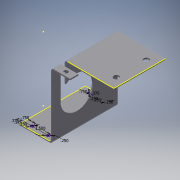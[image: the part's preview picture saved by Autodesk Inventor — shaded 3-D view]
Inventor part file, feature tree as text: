
AUTODESK INVENTOR PART (.ipt)
format: ipt  version: 2016 (Build 200138000, 138)  size: 217,088 bytes
history: native  units: in
note: dims shown in document units (in); Inventor stores cm internally (conversion verified against a paired STEP export)
features: sketch x12, sheet_metal_op x10, other x10, hole x1
ambient origin geometry x8: Origin, YZ Plane, XZ Plane, XY Plane, X Axis, Y Axis, Z Axis, Center Point
bodies: Solid1 (feature_tree)
feature tree (33):
  sheet_metal_op  "Face1"
  sheet_metal_op  "Flange1"
  sheet_metal_op  "Flange2"
  sketch  "Sketch6"  dims[d6=0.12in]
  sheet_metal_op  "Flange3"
  sketch  "Sketch11"  dims[d13=3.0in]
  sketch  "Sketch12"  dims[d14=3.75in d15=3.0in d16=0.12in d17=0.0in d18=0.5in d19=0.12in d20=0.0in d21=0.12in d22=0.06in d23=0.24in d24=0.12in d25=4.5in d26=90.0deg d27=0.12in d28=0.48in d29=0.12in d30=0.12in d34=0.12in d35=0.06in d36=0.24in d37=0.12in d38=1.75in d39=90.0deg d40=0.12in d41=0.48in d42=0.12in d43=0.12in d46=0.5in d47=0.75in d48=2.75in d49=0.12in d50=0.0in d51=0.375in d52=0.375in d53=0.75in d54=0.12in d55=0.0in d56=0.5in d57=0.75in d58=2.75in d59=0.12in d60=0.0in d61=0.25in d62=0.25in d63=1.5in d64=0.375in d65=0.375in d67=0.75in d68=0.375in d69=0.25in d70=0.75in d71=0.25in d72=0.25in d73=0.25in d74=0.375in d75=2.25in d76=0.12in d77=0.0in d78=0.25in d79=0.75in d80=0.375in d81=0.25in d82=0.5635in d83=0.12in d84=0.8108in]
  hole  "Hole1"  [1 undecoded]
  sketch  "Sketch1"  dims[d0=6.0in d1=3.0in]
  other  "Plate1"
  sketch  "Sketch2"  dims[d2=0.12in]
  other  "Plate2"
  sheet_metal_op  "Bend1"
  sheet_metal_op  "Corner1"
  sketch  "Sketch3"  dims[d3=0.12in]
  sketch  "Sketch4"  dims[d4=0.06in]
  sketch  "Sketch5"  dims[d5=0.24in]
  other  "Plate3"
  sheet_metal_op  "Bend2"
  sheet_metal_op  "Corner2"
  sketch  "Sketch7"  dims[d7=6.0in d8=90.0deg d9=0.12in]
  other  "Plate4"
  sheet_metal_op  "Bend3"
  sheet_metal_op  "Corner3"
  sketch  "Sketch8"  dims[d10=0.48in]
  sketch  "Sketch9"  dims[d11=0.12in]
  sketch  "Sketch10"  dims[d12=0.12in]
  other  "Cut1"
  other  "Cut2"
  other  "Cut4"
  other  "Cut5"
  other  "Cut6"
  other  "Cut7"
note: 1 required parameter value undecoded (feature->parameter linkage not recoverable at this tier; creation-order binding heuristic only, values carry confidence <= 0.55)
